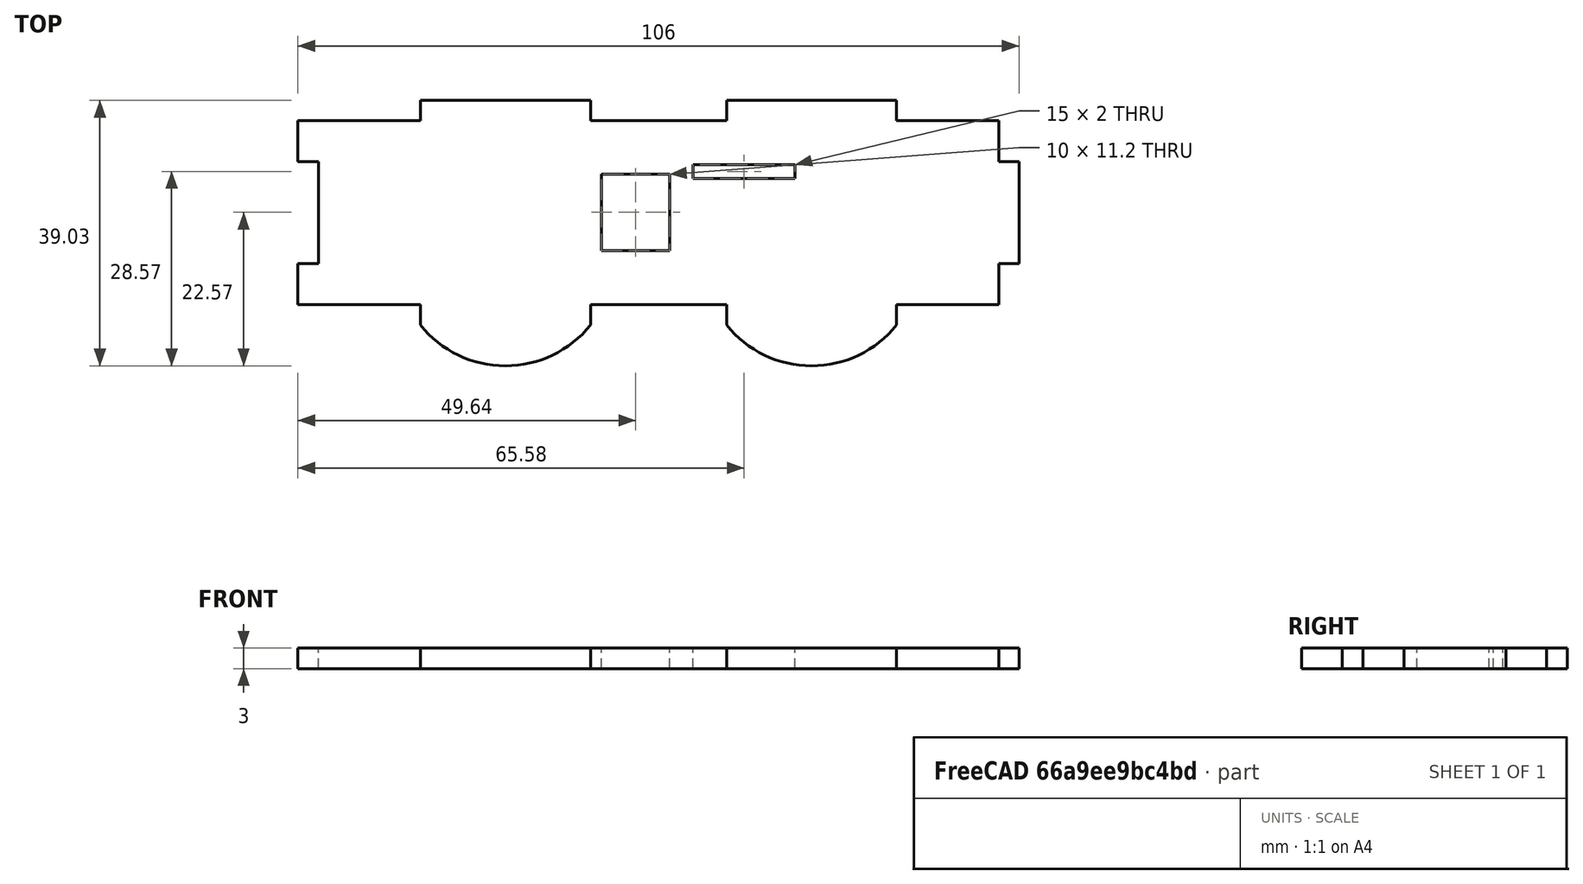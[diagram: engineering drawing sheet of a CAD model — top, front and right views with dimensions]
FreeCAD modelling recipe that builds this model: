
FCSTD DOCUMENT  (FreeCAD 0.19R24267 +99 (Git))
Label: side4
License: All rights reserved
LicenseURL: http://en.wikipedia.org/wiki/All_rights_reserved
objects: App::Part×1, Sketcher::SketchObject×1, Part::Extrusion×1
note: 2 computed .brp shape members not serialized (recipe doc carries the construction recipe); baked Part::Feature solids carry a one-line shape summary decoded from their .brp

FEATURE [App::Part] Part
  Origin = -> Origin
FEATURE [Sketcher::SketchObject] Sketch
  FullyConstrained = false
  sketch-geometry (56):
    g0: LineSegment StartX=0 StartY=0 StartZ=0 EndX=100 EndY=0 EndZ=0
    g1: LineSegment StartX=100 StartY=0 StartZ=0 EndX=100 EndY=1.6 EndZ=0
    g2: LineSegment StartX=100 StartY=1.6 StartZ=0 EndX=0 EndY=1.6 EndZ=0
    g3: LineSegment StartX=0 StartY=1.6 StartZ=0 EndX=0 EndY=0 EndZ=0
    g4: LineSegment StartX=0 StartY=-6.37 StartZ=0 EndX=100 EndY=-6.37 EndZ=0
    g5: LineSegment StartX=100 StartY=-6.37 StartZ=0 EndX=100 EndY=20.66 EndZ=0
    g6: LineSegment StartX=100 StartY=20.66 StartZ=0 EndX=0 EndY=20.66 EndZ=0
    g7: LineSegment StartX=0 StartY=20.66 StartZ=0 EndX=0 EndY=-6.37 EndZ=0
    g8: LineSegment StartX=15 StartY=-6.37 StartZ=0 EndX=40 EndY=-6.37 EndZ=0
    g9: LineSegment StartX=40 StartY=-6.37 StartZ=0 EndX=40 EndY=-9.37 EndZ=0
    g10: LineSegment StartX=40 StartY=-9.37 StartZ=0 EndX=15 EndY=-9.37 EndZ=0
    g11: LineSegment StartX=15 StartY=-9.37 StartZ=0 EndX=15 EndY=-6.37 EndZ=0
    g12: LineSegment StartX=60 StartY=-6.37 StartZ=0 EndX=85 EndY=-6.37 EndZ=0
    g13: LineSegment StartX=85 StartY=-6.37 StartZ=0 EndX=85 EndY=-9.37 EndZ=0
    g14: LineSegment StartX=85 StartY=-9.37 StartZ=0 EndX=60 EndY=-9.37 EndZ=0
    g15: LineSegment StartX=60 StartY=-9.37 StartZ=0 EndX=60 EndY=-6.37 EndZ=0
    g16: LineSegment StartX=15 StartY=20.66 StartZ=0 EndX=40 EndY=20.66 EndZ=0
    g17: LineSegment StartX=40 StartY=20.66 StartZ=0 EndX=40 EndY=23.66 EndZ=0
    g18: LineSegment StartX=40 StartY=23.66 StartZ=0 EndX=15 EndY=23.66 EndZ=0
    g19: LineSegment StartX=15 StartY=23.66 StartZ=0 EndX=15 EndY=20.66 EndZ=0
    g20: LineSegment StartX=60 StartY=20.66 StartZ=0 EndX=85 EndY=20.66 EndZ=0
    g21: LineSegment StartX=85 StartY=20.66 StartZ=0 EndX=85 EndY=23.66 EndZ=0
    g22: LineSegment StartX=85 StartY=23.66 StartZ=0 EndX=60 EndY=23.66 EndZ=0
    g23: LineSegment StartX=60 StartY=23.66 StartZ=0 EndX=60 EndY=20.66 EndZ=0
    g24: LineSegment StartX=100 StartY=14.66 StartZ=0 EndX=103 EndY=14.66 EndZ=0
    g25: LineSegment StartX=103 StartY=14.66 StartZ=0 EndX=103 EndY=-0.34 EndZ=0
    g26: LineSegment StartX=103 StartY=-0.34 StartZ=0 EndX=100 EndY=-0.34 EndZ=0
    g27: LineSegment StartX=100 StartY=-0.34 StartZ=0 EndX=100 EndY=14.66 EndZ=0
    g28: LineSegment StartX=0 StartY=-0.34 StartZ=0 EndX=0 EndY=14.66 EndZ=0
    g29: LineSegment StartX=0 StartY=20.66 StartZ=0 EndX=15 EndY=20.66 EndZ=0
    g30: LineSegment StartX=40 StartY=20.66 StartZ=0 EndX=60 EndY=20.66 EndZ=0
    g31: LineSegment StartX=85 StartY=20.66 StartZ=0 EndX=100 EndY=20.66 EndZ=0
    g32: LineSegment StartX=100 StartY=-0.34 StartZ=0 EndX=100 EndY=-6.37 EndZ=0
    g33: LineSegment StartX=100 StartY=-6.37 StartZ=0 EndX=85 EndY=-6.37 EndZ=0
    g34: LineSegment StartX=60 StartY=-6.37 StartZ=0 EndX=40 EndY=-6.37 EndZ=0
    g35: LineSegment StartX=15 StartY=-6.37 StartZ=0 EndX=0 EndY=-6.37 EndZ=0
    g36: LineSegment StartX=100 StartY=20.66 StartZ=0 EndX=100 EndY=14.66 EndZ=0
    g37: ArcOfCircle CenterX=27.5 CenterY=0.650833 CenterZ=0 NormalX=0 NormalY=0 NormalZ=1 AngleXU=0 Radius=16.0208 StartAngle=3.81735 EndAngle=5.60743
    g38: GeomPoint X=27.5 Y=-15.37 Z=0
    g39: ArcOfCircle CenterX=72.5 CenterY=0.650833 CenterZ=0 NormalX=0 NormalY=0 NormalZ=1 AngleXU=0 Radius=16.0208 StartAngle=3.81735 EndAngle=5.60743
    g40: GeomPoint X=72.5 Y=-15.37 Z=0
    g41: LineSegment StartX=0 StartY=14.66 StartZ=0 EndX=-3 EndY=14.66 EndZ=0
    g42: LineSegment StartX=-3 StartY=-0.34 StartZ=0 EndX=0 EndY=-0.34 EndZ=0
    g43: LineSegment StartX=-3 StartY=-0.34 StartZ=0 EndX=-3 EndY=-6.37 EndZ=0
    g44: LineSegment StartX=-3 StartY=-6.37 StartZ=0 EndX=0 EndY=-6.37 EndZ=0
    g45: LineSegment StartX=-3 StartY=14.66 StartZ=0 EndX=-3 EndY=20.66 EndZ=0
    g46: LineSegment StartX=-3 StartY=20.66 StartZ=0 EndX=0 EndY=20.66 EndZ=0
    g47: LineSegment StartX=0 StartY=14.66 StartZ=0 EndX=0 EndY=-0.34 EndZ=0
    g48: LineSegment StartX=41.64 StartY=1.6 StartZ=0 EndX=51.64 EndY=1.6 EndZ=0
    g49: LineSegment StartX=51.64 StartY=1.6 StartZ=0 EndX=51.64 EndY=12.8 EndZ=0
    g50: LineSegment StartX=51.64 StartY=12.8 StartZ=0 EndX=41.64 EndY=12.8 EndZ=0
    g51: LineSegment StartX=41.64 StartY=12.8 StartZ=0 EndX=41.64 EndY=1.6 EndZ=0
    g52: LineSegment StartX=55.08 StartY=14.2 StartZ=0 EndX=70.08 EndY=14.2 EndZ=0
    g53: LineSegment StartX=70.08 StartY=14.2 StartZ=0 EndX=70.08 EndY=12.2 EndZ=0
    g54: LineSegment StartX=70.08 StartY=12.2 StartZ=0 EndX=55.08 EndY=12.2 EndZ=0
    g55: LineSegment StartX=55.08 StartY=12.2 StartZ=0 EndX=55.08 EndY=14.2 EndZ=0
  constraints (153):
    c: Coincident(g0,g1)
    c: Coincident(g1,g2)
    c: Coincident(g2,g3)
    c: Coincident(g3,g0)
    c: Horizontal(g0)
    c: Horizontal(g2)
    c: Vertical(g1)
    c: Vertical(g3)
    c: Coincident(g0,g-1)
    c: DistanceX(g2,g2) = 100
    c: DistanceY(g3,g3) = 1.6
    c: Coincident(g4,g5)
    c: Coincident(g5,g6)
    c: Coincident(g6,g7)
    c: Coincident(g7,g4)
    c: Horizontal(g4)
    c: Horizontal(g6)
    c: Vertical(g5)
    c: Vertical(g7)
    c: PointOnObject(g4,g-2)
    c: Equal(g6,g2)
    c: DistanceY(g2,g6) = 19.06
    c: DistanceY(g4,g-1) = 6.37
    c: Coincident(g8,g9)
    c: Coincident(g9,g10)
    c: Coincident(g10,g11)
    c: Coincident(g11,g8)
    c: Horizontal(g8)
    c: Horizontal(g10)
    c: Vertical(g9)
    c: Vertical(g11)
    c: PointOnObject(g8,g4)
    c: Coincident(g12,g13)
    c: Coincident(g13,g14)
    c: Coincident(g14,g15)
    c: Coincident(g15,g12)
    c: Horizontal(g12)
    c: Horizontal(g14)
    c: Vertical(g13)
    c: Vertical(g15)
    c: PointOnObject(g12,g4)
    c: Coincident(g16,g17)
    c: Coincident(g17,g18)
    c: Coincident(g18,g19)
    c: Coincident(g19,g16)
    c: Horizontal(g16)
    c: Horizontal(g18)
    c: Vertical(g17)
    c: Vertical(g19)
    c: PointOnObject(g16,g6)
    c: Coincident(g20,g21)
    c: Coincident(g21,g22)
    c: Coincident(g22,g23)
    c: Coincident(g23,g20)
    c: Horizontal(g20)
    c: Horizontal(g22)
    c: Vertical(g21)
    c: Vertical(g23)
    c: PointOnObject(g20,g6)
    c: Coincident(g24,g25)
    c: Coincident(g25,g26)
    c: Coincident(g26,g27)
    c: Coincident(g27,g24)
    c: Horizontal(g24)
    c: Horizontal(g26)
    c: Vertical(g25)
    c: Vertical(g27)
    c: PointOnObject(g24,g5)
    c: Vertical(g28)
    c: PointOnObject(g28,g7)
    c: Equal(g18,g22)
    c: Equal(g14,g10)
    c: DistanceX(g18,g18) = 25
    c: Equal(g11,g15)
    c: Equal(g15,g23)
    c: Equal(g23,g24)
    c: DistanceY(g23,g23) = 3
    c: DistanceX(g6,g18) = 15
    c: DistanceX(g21,g5) = 15
    c: DistanceX(g13,g4) = 15
    c: DistanceX(g4,g10) = 15
    c: Equal(g14,g22)
    c: DistanceY(g25,g25) = 15
    c: DistanceY(g24,g5) = 6
    c: Coincident(g29,g16)
    c: Coincident(g30,g16)
    c: Coincident(g30,g20)
    c: Coincident(g31,g20)
    c: Coincident(g31,g5)
    c: Coincident(g32,g26)
    c: Coincident(g32,g4)
    c: Coincident(g33,g32)
    c: Coincident(g33,g12)
    c: Coincident(g34,g12)
    c: Coincident(g34,g8)
    c: Coincident(g35,g8)
    c: Coincident(g35,g4)
    c: Coincident(g36,g31)
    c: Coincident(g36,g24)
    c: Coincident(g37,g9)
    c: Coincident(g37,g10)
    c: PointOnObject(g38,g37)
    c: DistanceY(g38,g9) = 6
    c: DistanceX(g38,g9) = 12.5
    c: Coincident(g39,g14)
    c: Coincident(g39,g13)
    c: PointOnObject(g40,g39)
    c: DistanceX(g40,g13) = 12.5
    c: DistanceY(g40,g13) = 6
    c: Coincident(g41,g28)
    c: Horizontal(g41)
    c: PointOnObject(g42,g7)
    c: Horizontal(g42)
    c: DistanceY(g42,g41) = 15
    c: DistanceX(g41,g41) = 3
    c: Horizontal(g41,g24)
    c: Vertical(g43)
    c: Coincident(g44,g43)
    c: Coincident(g44,g35)
    c: Horizontal(g44)
    c: Coincident(g45,g41)
    c: Vertical(g45)
    c: Coincident(g46,g29)
    c: Horizontal(g46)
    c: Horizontal(g29,g19)
    c: Coincident(g47,g41)
    c: Coincident(g47,g42)
    c: DistanceY(g45,g45) = 6
    c: Equal(g43,g32)
    c: Coincident(g48,g49)
    c: Coincident(g49,g50)
    c: Coincident(g50,g51)
    c: Coincident(g51,g48)
    c: Horizontal(g48)
    c: Horizontal(g50)
    c: Vertical(g49)
    c: Vertical(g51)
    c: PointOnObject(g48,g2)
    c: Coincident(g52,g53)
    c: Coincident(g53,g54)
    c: Coincident(g54,g55)
    c: Coincident(g55,g52)
    c: Horizontal(g52)
    c: Horizontal(g54)
    c: Vertical(g53)
    c: Vertical(g55)
    c: DistanceX(g50,g50) = 10
    c: DistanceX(g49,g1) = 48.36
    c: DistanceY(g51,g51) = 11.2
    c: DistanceX(g52,g52) = 15
    c: DistanceX(g52,g1) = 29.92
    c: DistanceY(g53,g53) = 2
    c: DistanceY(g1,g53) = 10.6
FEATURE [Part::Extrusion] Extrude
  Base = -> Sketch
  Dir = (0,0,1)
  DirMode = 2
  FaceMakerClass = Part::FaceMakerBullseye
  LengthFwd = 3
  LengthRev = 0
  Solid = true
  Symmetric = false
